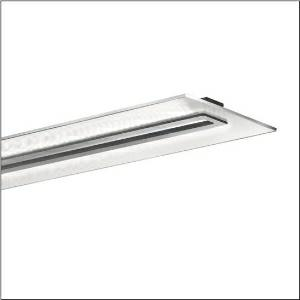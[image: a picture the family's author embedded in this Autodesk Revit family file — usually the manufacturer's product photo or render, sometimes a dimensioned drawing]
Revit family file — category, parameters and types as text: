
# Revit family: vega_11_5mn238dle
name_source: partatom
category: Lighting Fixtures
units: mm (PartAtom-declared; Revit-internal decimal feet)

## family parameters
Cut with Voids When Loaded = No
Host = Face
Light Source = No
Part Type = Normal
Room Calculation Point = No
Round Connector Dimension = Use Diameter
Shared = No

## types (1)
- --- (1 x LED 4000K / CRI = 80 (unbekannt), 8130 lm, 4000K)
    Apparent Load = 62 VA
    CIE Flux Codes = 61 86 97 62 100
    Color Rendering = 80
    Color Temperature = 4000K
    Default Elevation = 1800 mm
    Description = Vega 11, office luminaire, primary light control with prismatic reflector, of PMMA, transparent prismatic structure, CAT 2 (L<= 1500cd/m²), light emission: direct/indirect distribution, primary light characteristic: symmetric, installation type: suspended mounting, surface-mounted, LED, rated luminous flux: 8.130lm, luminous efficacy: 131lm/W, light colour: 840, colour temperature: 4000K, control gear: DALI, with terminal, 3+2-pole, max. 2.5mm², mains connection: 230V, AC, 50Hz, connection cable inclusive, cable length: 1,5m, rated input power: 62W, luminaire housing, rectangular, rounded, of aluminium section, anodised, metallic grey (RAL 9006), length: 1.250mm, width: 350mm, height: 43mm, luminaire housing, lower part, of aluminium section, anodised, metallic grey (RAL 9006), of PC, grey, protection rating (complete): IP20, insulation class (complete): insulation class I (protective earthing), certification: CE, standard: EN 50419, packaging unit: 1 piece
    Height = 40 mm  [stored 0.131234 ft]
    Lamp = 1 x LED 4000K / CRI >= 80 (unbekannt)
    Lamp Light Flux = 8130 lm
    Lamp count = 1
    Length = 1250 mm
    Luminous efficacy = 131 lm/W
    Manufacturer = Siteco
    ModVariant = No
    Model = 5MN238DLE
    Mounting Place = Ceiling
    Mounting Type = Pendant
    Number of Poles = 1
    OnlyDefault = Yes
    Power Factor = 1
    Product Name = Vega 11
    Product group = office luminaire | ceiling pendant
    ProductGroupID = 903
    Protection Class = Protection class I
    Protection Degree = IP 20
    RLX_Detail_Level = 1
    RLX_Emergency_Light_Flux = 0 lm
    RLX_Emergency_Type = 0
    RLX_Emergency_Type_DB = No
    RlxData = <blob elided: 62765 chars, md5=a84c4cb0>
    Socket = socket
    Standby Power = 0 W
    System Light Flux = 8130 lm
    System Power = 62 W
    Type Comments = factory setting: luminous flux: 100 % | dim-lin: 254 | 458 mA
    Type Image = l_1004807.jpg
    URL = http://relux.com
    VarID = @adj_197183
    Voltage = 0 V
    Weight = 0.00 kg
    Width = 350 mm

note: [stored X ft] marks values corroborated as IEEE doubles in the binary element streams (Revit-internal decimal feet)

## geometry (parser evidence)
native form markers: Blend x4, Sweep x12
no freeform markers — native parametric forms only
